# Revit family: IS_ConnectBlue_A5933_BIM_DE
name_source: partatom
category: Plumbing Fixtures
revit_build: Autodesk Revit MEP 2014 (Build: 20130308_1515(x64)
units: mm (PartAtom-declared; Revit-internal decimal feet)

## types (1)
- A5933AA - Connect Blue wall single lever basin mixer
    Accessories = www.idealstandard.de\ersatzteile
    AreaUnits = millimeters
    Assembly Code = C1030200
    AssetType = Fixed
    BIMObjectName = ISI_IdealStandard_WashbasinTaps_ConnectBlue_A5933AA
    BarCode = 4015413315739
    Brand = Ideal Standard
    CWFU = 0
    Category = SanitaryTerminal_FAUCET
    CodePerformance = EN 817, DIN 4109
    Color = Chrome
    ConnectionType = Plumbing
    Cost = 0 $
    Default Elevation = 800 mm  [stored 2.62467 ft]
    Description = Connect Blue wall single lever basin mixer
    DurationUnit = year
    ExpectedLife = 25
    FaucetFunction = MIXED
    FaucetOperation = LEVERHANDLE
    FaucetType = PILLAR
    Features = Connect Blue wall single lever basin mixer
    Finish = chrome
    HWFU = 0
    IfcExportAs = IfcValveType
    IfcExportType = FAUCET
    InstallationInstructions = www.idealstandard.de/produkte
    LinearUnits = millimeters
    ManufacturerURL = www.idealstandard.de
    Material = Brass
    Model = A5933AA
    ModelNumber = A5933AA
    ModelReference = Connect Blue wall single lever basin mixer
    NBSDescription = Water supply fittings for wash basins and troughs
    NBSReference = 45-35-70/371
    Name = WashbasinTaps_ConnectBlue_A5933AA_IdealStandard
    NettWeight = 1,36 kg
    NominalHeight = 128 mm
    NominalLength = 213 mm
    NominalWidth = 55 mm
    ProductInformation = www.idealstandard.de/produkte
    Shape = Sculptured
    Size = 215x345x85mm
    Space = Internal
    SpareParts = www.idealstandard.de/ersatzteile
    TMV3 = Yes
    TestPressure = 10 Bar
    URL = www.idealstandard.com
    Uniclass2015Code = Pr_40_20_87_98
    Uniclass2015Title = Washbasin taps
    Uniclass2015Version = Products v1.1
    Version = 1
    VolumeUnits = Litres
    WFU = 0
    WarrantyDescription = Manufacturers Warranty
    WarrantyDurationUnit = year
    WorkingPressure = 1-5 Bar

note: [stored X ft] marks values corroborated as IEEE doubles in the binary element streams (Revit-internal decimal feet)

## geometry (parser evidence)
native form markers: Sweep x4
no freeform markers — native parametric forms only
